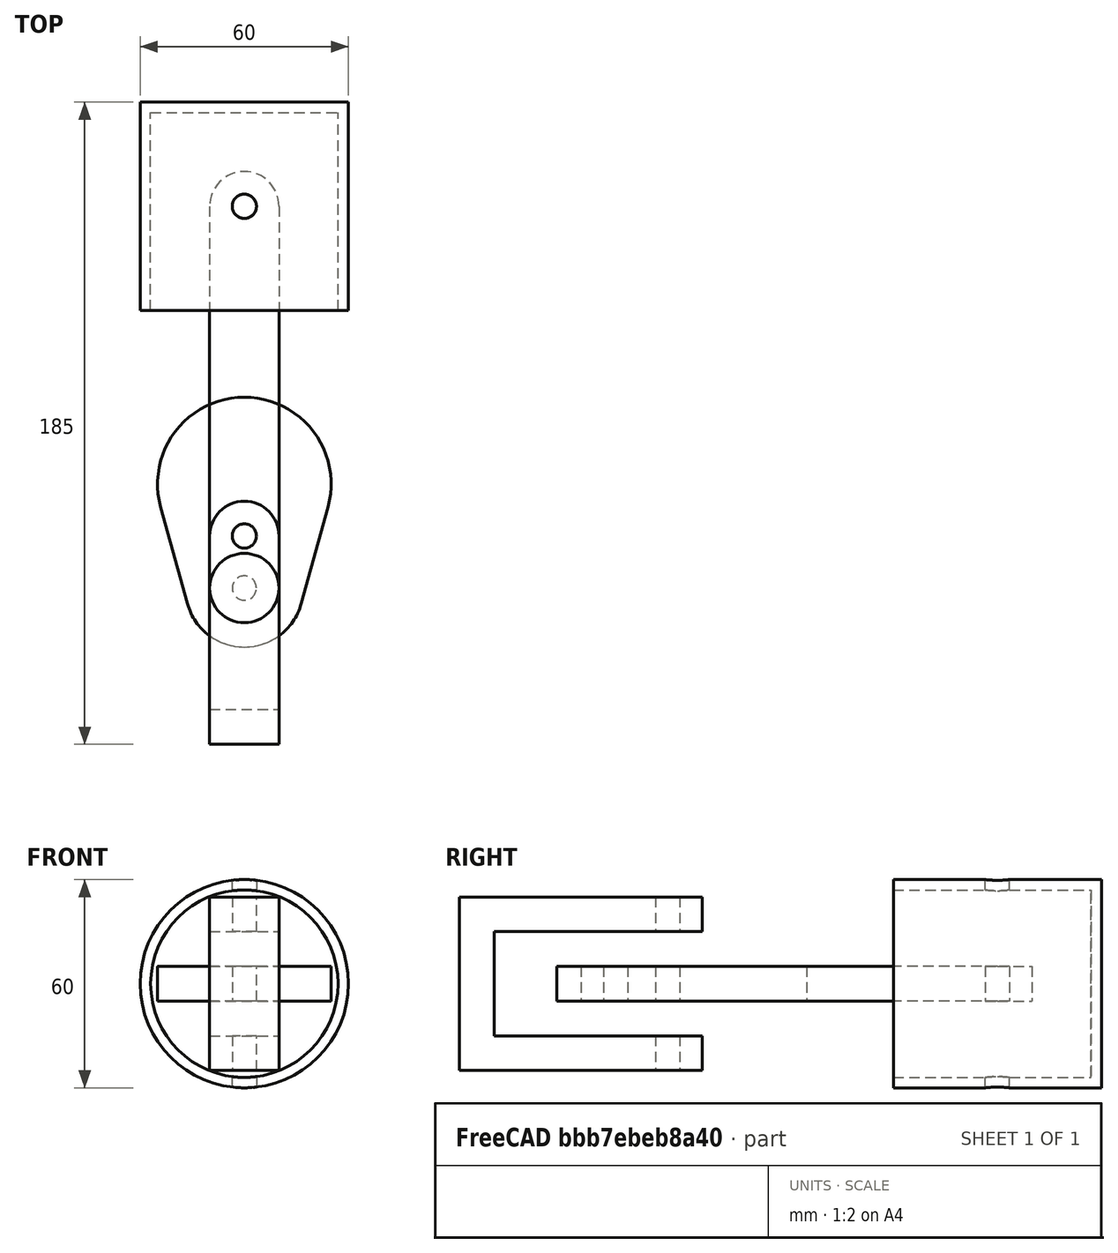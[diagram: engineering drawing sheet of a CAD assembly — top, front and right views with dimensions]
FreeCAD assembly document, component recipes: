
FREECAD ASSEMBLY — COMPONENT RECIPES ("piston head")

This assembly document has 5 components, labeled P0..P4 below (a component is one placed body or linked part). 5 of them carry a construction recipe — the FreeCAD feature program that regenerates the part from scratch, quoted from this document or its linked companion documents; the rest are supplied as boundary geometry only. No exploded tour is included for this assembly.
COMPONENT P0 — recipe-attached ("crank001", modeled in this document).
Construction recipe (the document's own serialized feature program — sketch geometry with constraints, then the solid features built on it; lengths are millimeters unless a unit is written):

FEATURE [PartDesign::SubShapeBinder] Binder002
  BindCopyOnChange = 0
  BindMode = 0
  ClaimChildren = false
  Context = -> Body002 [Binder002.]
  Fuse = false
  MakeFace = false
  OffsetFill = false
  OffsetIntersection = false
  OffsetJoinType = 0
  OffsetOpenResult = false
  PartialLoad = false
  Refine = true
  Relative = true
  Support = -> [Sketch]
  _Version = 2
FEATURE [Sketcher::SketchObject] Sketch004
  ArcFitTolerance = 1e-06
  AttachmentSupport = -> [XY_Plane002]
  ExternalGeometry = -> [Binder002]
  FullyConstrained = true
  MakeInternals = false
  MapMode = 5
  sketch-geometry (6):
    g0: Circle CenterX=0 CenterY=-40 CenterZ=0 NormalX=0 NormalY=0 NormalZ=1 AngleXU=0 Radius=3.5
    g1: Circle CenterX=0 CenterY=-55 CenterZ=0 NormalX=0 NormalY=0 NormalZ=1 AngleXU=0 Radius=3.5
    g2: LineSegment StartX=-24.0947 StartY=-31.6667 StartZ=0 EndX=-16.3844 EndY=-59.5333 EndZ=0
    g3: ArcOfCircle CenterX=-2.1e-15 CenterY=-55 CenterZ=0 NormalX=0 NormalY=0 NormalZ=1 AngleXU=0 Radius=17 StartAngle=3.41153 EndAngle=6.01325
    g4: LineSegment StartX=16.3844 StartY=-59.5333 StartZ=0 EndX=24.0947 EndY=-31.6667 EndZ=0
    g5: ArcOfCircle CenterX=-7e-16 CenterY=-25 CenterZ=0 NormalX=0 NormalY=0 NormalZ=1 AngleXU=0 Radius=25 StartAngle=6.01325 EndAngle=9.69471
  constraints (12):
    c: Coincident(g0,g-8)
    c: Equal(g0,g-8)
    c: Coincident(g1,g-7)
    c: Equal(g1,g-7)
    c: Coincident(g-4,g2)
    c: Coincident(g2,g-5)
    c: Tangent(g2,g3) = -1.5708
    c: Coincident(g3,g-6)
    c: Tangent(g3,g4) = -1.5708
    c: Tangent(g4,g5) = -1.5708
    c: Coincident(g5,g2)
    c: Equal(g5,g-3)
FEATURE [PartDesign::Pad] Pad001
  Direction = (0,0,1)
  Length = 10
  Length2 = 10
  Midplane = true
  Profile = -> Sketch004
  ReferenceAxis = -> Sketch004 [N_Axis]
  Refine = true
  Suppressed = false
  Type = 0
FEATURE [PartDesign::Body] Body002  label="crank"
  AllowCompound = false
  Group = -> [Binder002,Sketch004,Pad001]
  Origin = -> Origin002
  Tip = -> Pad001
COMPONENT P1 — same part as P0; its construction recipe is shown at P0.
COMPONENT P2 — recipe-attached ("link001", modeled in this document).
Construction recipe (the document's own serialized feature program — sketch geometry with constraints, then the solid features built on it; lengths are millimeters unless a unit is written):

FEATURE [PartDesign::SubShapeBinder] Binder
  BindCopyOnChange = 0
  BindMode = 0
  ClaimChildren = false
  Context = -> Body [Binder.]
  Fuse = false
  MakeFace = true
  OffsetFill = false
  OffsetIntersection = false
  OffsetJoinType = 0
  OffsetOpenResult = false
  PartialLoad = false
  Refine = true
  Relative = true
  Support = -> [Sketch]
  _Version = 2
FEATURE [Sketcher::SketchObject] Sketch001
  ArcFitTolerance = 1e-06
  AttachmentSupport = -> [XY_Plane]
  ExternalGeometry = -> [Binder]
  FullyConstrained = true
  MakeInternals = false
  MapMode = 5
  sketch-geometry (6):
    g0: LineSegment StartX=-10 StartY=55 StartZ=0 EndX=-10 EndY=-55 EndZ=0
    g1: LineSegment StartX=10 StartY=55 StartZ=0 EndX=10 EndY=-55 EndZ=0
    g2: Circle CenterX=-4e-16 CenterY=55 CenterZ=0 NormalX=0 NormalY=0 NormalZ=1 AngleXU=0 Radius=3.5
    g3: Circle CenterX=7e-16 CenterY=-55 CenterZ=0 NormalX=0 NormalY=0 NormalZ=1 AngleXU=0 Radius=3.5
    g4: ArcOfCircle CenterX=7e-16 CenterY=-55 CenterZ=0 NormalX=0 NormalY=0 NormalZ=1 AngleXU=0 Radius=10 StartAngle=3.14159 EndAngle=6.28319
    g5: ArcOfCircle CenterX=-4e-16 CenterY=55 CenterZ=0 NormalX=0 NormalY=0 NormalZ=1 AngleXU=0 Radius=10 StartAngle=6.28318 EndAngle=9.42478
  constraints (14):
    c: Coincident(g-4,g0)
    c: Coincident(g0,g-5)
    c: Coincident(g-6,g1)
    c: Coincident(g1,g-6)
    c: Coincident(g4,g3)
    c: Coincident(g4,g0)
    c: Coincident(g4,g1)
    c: Equal(g-7,g2)
    c: Equal(g-8,g3)
    c: Equal(g4,g-5)
    c: Coincident(g5,g2)
    c: Coincident(g5,g0)
    c: Coincident(g5,g1)
    c: Equal(g-3,g5)
FEATURE [PartDesign::Pad] Pad
  Direction = (0,0,1)
  Length = 10
  Length2 = 10
  Midplane = true
  Profile = -> Sketch001
  ReferenceAxis = -> Sketch001 [N_Axis]
  Refine = true
  Suppressed = false
  Type = 0
FEATURE [PartDesign::Body] Body  label="link"
  AllowCompound = false
  Group = -> [Binder,Sketch001,Pad]
  Origin = -> Origin
  Tip = -> Pad
COMPONENT P3 — recipe-attached ("mmount002", modeled in this document).
Construction recipe (the document's own serialized feature program — sketch geometry with constraints, then the solid features built on it; lengths are millimeters unless a unit is written):

FEATURE [PartDesign::SubShapeBinder] Binder003
  BindCopyOnChange = 0
  BindMode = 0
  ClaimChildren = false
  Context = -> Body003 [Binder003.]
  Fuse = false
  MakeFace = false
  OffsetFill = false
  OffsetIntersection = false
  OffsetJoinType = 0
  OffsetOpenResult = false
  PartialLoad = false
  Refine = true
  Relative = true
  Support = -> [Sketch]
  _Version = 2
FEATURE [Sketcher::SketchObject] Sketch005
  ArcFitTolerance = 1e-06
  AttachmentSupport = -> [XY_Plane003]
  ExternalGeometry = -> [Binder003]
  FullyConstrained = true
  MakeInternals = false
  MapMode = 5
  sketch-geometry (7):
    g0: LineSegment StartX=-10 StartY=-55 StartZ=0 EndX=-10 EndY=-100 EndZ=0
    g1: LineSegment StartX=-10 StartY=-100 StartZ=0 EndX=10 EndY=-100 EndZ=0
    g2: LineSegment StartX=10 StartY=-55 StartZ=0 EndX=10 EndY=-100 EndZ=0
    g3: LineSegment StartX=10 StartY=-40 StartZ=0 EndX=10 EndY=-55 EndZ=0
    g4: LineSegment StartX=-10 StartY=-40 StartZ=0 EndX=-10 EndY=-55 EndZ=0
    g5: Circle CenterX=-1.2e-15 CenterY=-40 CenterZ=0 NormalX=0 NormalY=0 NormalZ=1 AngleXU=0 Radius=3.5
    g6: ArcOfCircle CenterX=-1.2e-15 CenterY=-40 CenterZ=0 NormalX=0 NormalY=0 NormalZ=1 AngleXU=0 Radius=10 StartAngle=-1.52967e-10 EndAngle=3.14159
  constraints (14):
    c: Coincident(g0,g-7)
    c: Coincident(g0,g-5)
    c: Coincident(g1,g0)
    c: Coincident(g1,g-4)
    c: Coincident(g2,g-8)
    c: Coincident(g2,g1)
    c: Coincident(g3,g-6)
    c: Coincident(g3,g2)
    c: Coincident(g4,g-6)
    c: Coincident(g4,g0)
    c: Tangent(g4,g6) = -1.5708
    c: Coincident(g6,g3)
    c: Coincident(g5,g6)
    c: Equal(g-9,g5)
FEATURE [PartDesign::Pad] Pad002
  Direction = (0,0,1)
  Length = 50
  Length2 = 10
  Midplane = true
  Profile = -> Sketch005
  ReferenceAxis = -> Sketch005 [N_Axis]
  Refine = true
  Suppressed = false
  Type = 0
FEATURE [Sketcher::SketchObject] Sketch006
  ArcFitTolerance = 1e-06
  AttachmentSupport = -> [Pad002]
  ExternalGeometry = -> [Pad002]
  FullyConstrained = true
  MakeInternals = false
  MapMode = 5
  Placement = pos=(-10,4.689e-13,0) rot=(-0.57735,0.57735,0.57735;4.18879rad)
  sketch-geometry (4):
    g0: LineSegment StartX=25 StartY=15 StartZ=0 EndX=25 EndY=-15 EndZ=0
    g1: LineSegment StartX=25 StartY=-15 StartZ=0 EndX=90 EndY=-15 EndZ=0
    g2: LineSegment StartX=90 StartY=-15 StartZ=0 EndX=90 EndY=15 EndZ=0
    g3: LineSegment StartX=90 StartY=15 StartZ=0 EndX=25 EndY=15 EndZ=0
  constraints (12):
    c: Coincident(g0,g1)
    c: Coincident(g1,g2)
    c: Coincident(g2,g3)
    c: Coincident(g3,g0)
    c: Vertical(g0)
    c: Vertical(g2)
    c: Horizontal(g1)
    c: Horizontal(g3)
    c: Distance(g-4,g3) = 10
    c: Distance(g1,g3) = 30
    c: Distance(g-3,g2) = 10
    c: DistanceX(g3,g3) = 65
FEATURE [PartDesign::Pocket] Pocket001
  BaseFeature = -> Pad002
  Direction = (1,-4.67e-14,-1e-16)
  Length = 10
  Length2 = 5
  Midplane = true
  Profile = -> Sketch006
  ReferenceAxis = -> Sketch006 [N_Axis]
  Refine = true
  Suppressed = false
  Type = 1
FEATURE [PartDesign::Body] Body003  label="mmount"
  AllowCompound = false
  Group = -> [Binder003,Sketch005,Pad002,Sketch006,Pocket001]
  Origin = -> Origin003
  Tip = -> Pocket001
COMPONENT P4 — recipe-attached ("piston head001", modeled in this document).
Construction recipe (the document's own serialized feature program — sketch geometry with constraints, then the solid features built on it; lengths are millimeters unless a unit is written):

FEATURE [PartDesign::SubShapeBinder] Binder001
  BindCopyOnChange = 0
  BindMode = 0
  ClaimChildren = false
  Context = -> Body001 [Binder001.]
  Fuse = false
  MakeFace = true
  OffsetFill = false
  OffsetIntersection = false
  OffsetJoinType = 0
  OffsetOpenResult = false
  PartialLoad = false
  Refine = true
  Relative = true
  Support = -> [Sketch]
  _Version = 2
FEATURE [Sketcher::SketchObject] Sketch002
  ArcFitTolerance = 1e-06
  AttachmentSupport = -> [XY_Plane001]
  ExternalGeometry = -> [Binder001]
  FullyConstrained = true
  MakeInternals = false
  MapMode = 5
  sketch-geometry (6):
    g0: LineSegment StartX=0 StartY=85 StartZ=0 EndX=-30 EndY=85 EndZ=0
    g1: LineSegment StartX=-30 StartY=85 StartZ=0 EndX=-30 EndY=25 EndZ=0
    g2: LineSegment StartX=-27 StartY=25 StartZ=0 EndX=-27 EndY=82 EndZ=0
    g3: LineSegment StartX=-27 StartY=82 StartZ=0 EndX=0 EndY=82 EndZ=0
    g4: LineSegment StartX=0 StartY=82 StartZ=0 EndX=0 EndY=85 EndZ=0
    g5: LineSegment StartX=-30 StartY=25 StartZ=0 EndX=-27 EndY=25 EndZ=0
  constraints (15):
    c: Symmetric(g-3,g-3,g0)
    c: Coincident(g0,g-4)
    c: Coincident(g1,g0)
    c: Coincident(g1,g-5)
    c: Vertical(g2)
    c: Coincident(g3,g2)
    c: PointOnObject(g3,g-2)
    c: Horizontal(g3)
    c: Coincident(g4,g3)
    c: Coincident(g4,g0)
    c: DistanceY(g4,g4) = 3
    c: DistanceX(g1,g2) = 3
    c: PointOnObject(g2,g-5)
    c: Coincident(g5,g1)
    c: Coincident(g5,g2)
FEATURE [PartDesign::Revolution] Revolution
  Angle = 360
  Angle2 = 60
  Axis = (0,1,0)
  Base = (0,0,0)
  Profile = -> Sketch002
  ReferenceAxis = -> Sketch002 [V_Axis]
  Refine = true
  Suppressed = false
  Type = 0
FEATURE [Sketcher::SketchObject] Sketch003
  ArcFitTolerance = 1e-06
  AttachmentSupport = -> [XY_Plane001]
  ExternalGeometry = -> [Binder001]
  FullyConstrained = true
  MakeInternals = false
  MapMode = 5
  sketch-geometry (1):
    g0: Circle CenterX=0 CenterY=55 CenterZ=0 NormalX=0 NormalY=0 NormalZ=1 AngleXU=0 Radius=3.5
  constraints (2):
    c: Coincident(g0,g-3)
    c: Equal(g0,g-3)
FEATURE [PartDesign::Pocket] Pocket
  BaseFeature = -> Revolution
  Direction = (0,0,-1)
  Length = 4
  Length2 = 5
  Midplane = true
  Profile = -> Sketch003
  ReferenceAxis = -> Sketch003 [N_Axis]
  Refine = true
  Suppressed = false
  Type = 1
FEATURE [PartDesign::Body] Body001  label="piston head"
  AllowCompound = false
  Group = -> [Binder001,Sketch002,Revolution,Sketch003,Pocket]
  Origin = -> Origin001
  Tip = -> Pocket
PROVENANCE & LICENSES
A FreeCAD (.FCStd) document from a public repository crawl; recipes are the document's own serialized feature recipes (and, for linked parts, companion documents' recipes).
License: as declared in the source repository (recorded in the dataset sidecar).
